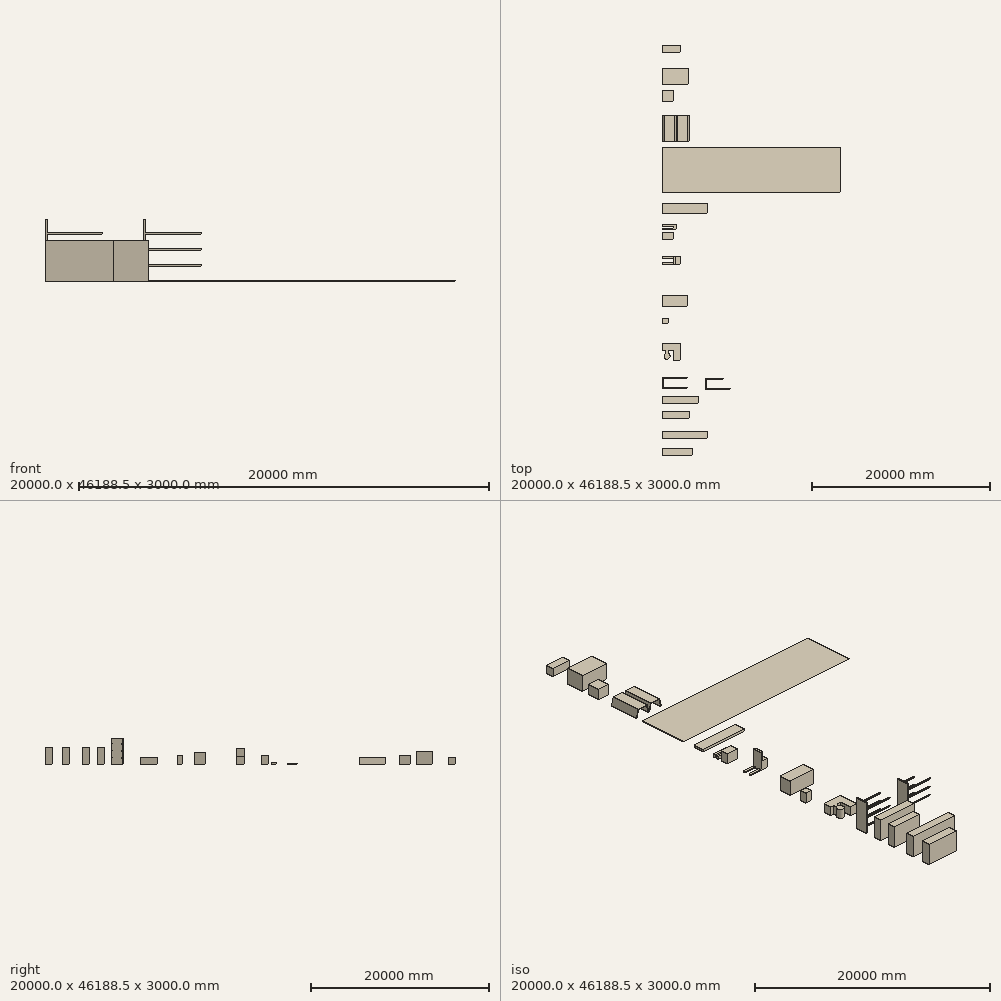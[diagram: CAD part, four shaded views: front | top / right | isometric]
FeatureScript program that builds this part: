
annotation { "Feature Type Name" : "Feature", "Feature Type Description" : "" }
export const myFeature = defineFeature(function(context is Context, id is Id, definition is map)
    precondition{}
    {
        {
            var Q0;
            Q0=qCreatedBy(makeId("Top.planeOp"),FACE);
            var sketch = newSketch(context, id + "F0", { "sketchPlane" : qUnion([Q0])});
            skLineSegment(sketch, "E0.bottom", {"start": v(0, 0) * mm, "end": v(3300, 0) * mm});
            skLineSegment(sketch, "E0.top", {"start": v(0, 800) * mm, "end": v(3300, 800) * mm});
            skLineSegment(sketch, "E0.left", {"start": v(0, 0) * mm, "end": v(0, 800) * mm});
            skLineSegment(sketch, "E0.right", {"start": v(3300, 0) * mm, "end": v(3300, 800) * mm});
            skLineSegment(sketch, "E1", {"start": v(0, 0) * mm, "end": v(0, 21740.58) * mm, "construction": true});
            skLineSegment(sketch, "E2.bottom", {"start": v(0, 1903.16) * mm, "end": v(5020, 1903.16) * mm});
            skLineSegment(sketch, "E2.top", {"start": v(0, 2703.16) * mm, "end": v(5020, 2703.16) * mm});
            skLineSegment(sketch, "E2.left", {"start": v(0, 1903.16) * mm, "end": v(0, 2703.16) * mm});
            skLineSegment(sketch, "E2.right", {"start": v(5020, 1903.16) * mm, "end": v(5020, 2703.16) * mm});
            skLineSegment(sketch, "E3.bottom", {"start": v(0, 4207.9) * mm, "end": v(3010, 4207.9) * mm});
            skLineSegment(sketch, "E3.top", {"start": v(0, 4907.9) * mm, "end": v(3010, 4907.9) * mm});
            skLineSegment(sketch, "E3.left", {"start": v(0, 4207.9) * mm, "end": v(0, 4907.9) * mm});
            skLineSegment(sketch, "E3.right", {"start": v(3010, 4207.9) * mm, "end": v(3010, 4907.9) * mm});
            skLineSegment(sketch, "E4.bottom", {"start": v(0, 5836.08) * mm, "end": v(4010, 5836.08) * mm});
            skLineSegment(sketch, "E4.top", {"start": v(0, 6636.08) * mm, "end": v(4010, 6636.08) * mm});
            skLineSegment(sketch, "E4.left", {"start": v(0, 5836.08) * mm, "end": v(0, 6636.08) * mm});
            skLineSegment(sketch, "E4.right", {"start": v(4010, 5836.08) * mm, "end": v(4010, 6636.08) * mm});
            skLineSegment(sketch, "E5.bottom", {"start": v(0, 7509.41) * mm, "end": v(2800, 7509.41) * mm});
            skLineSegment(sketch, "E5.top", {"start": v(0, 8769.41) * mm, "end": v(2800, 8769.41) * mm});
            skLineSegment(sketch, "E5.left", {"start": v(0, 7509.41) * mm, "end": v(0, 8769.41) * mm});
            skLineSegment(sketch, "E5.right", {"start": v(2800, 7509.41) * mm, "end": v(2800, 8769.41) * mm});
            skLineSegment(sketch, "E6", {"start": v(0, 11853.92) * mm, "end": v(342.53, 11853.92) * mm});
            skLineSegment(sketch, "E7", {"start": v(1200, 11853.92) * mm, "end": v(1200, 10653.92) * mm});
            skLineSegment(sketch, "E8", {"start": v(1200, 10653.92) * mm, "end": v(2000, 10653.92) * mm});
            skLineSegment(sketch, "E9", {"start": v(2000, 10653.92) * mm, "end": v(2000, 12653.92) * mm});
            skLineSegment(sketch, "E10", {"start": v(2000, 12653.92) * mm, "end": v(0, 12653.92) * mm});
            skLineSegment(sketch, "E11", {"start": v(0, 12653.92) * mm, "end": v(0, 11853.92) * mm});
            skArc(sketch, "E12", {"start": v(342.53, 11484.65) * mm, "mid": v(513.67, 10838.01) * mm, "end": v(624.53, 11497.66) * mm});
            skLineSegment(sketch, "E13", {"start": v(342.53, 11853.92) * mm, "end": v(342.53, 11484.65) * mm});
            skLineSegment(sketch, "E14", {"start": v(624.53, 11497.66) * mm, "end": v(624.53, 11853.92) * mm});
            skLineSegment(sketch, "E15.trimOffspring", {"start": v(624.53, 11853.92) * mm, "end": v(1200, 11853.92) * mm});
            skLineSegment(sketch, "E16.bottom", {"start": v(0, 14846.44) * mm, "end": v(630, 14846.44) * mm});
            skLineSegment(sketch, "E16.top", {"start": v(0, 15476.44) * mm, "end": v(630, 15476.44) * mm});
            skLineSegment(sketch, "E16.left", {"start": v(0, 14846.44) * mm, "end": v(0, 15476.44) * mm});
            skLineSegment(sketch, "E16.right", {"start": v(630, 14846.44) * mm, "end": v(630, 15476.44) * mm});
            skLineSegment(sketch, "E17.bottom", {"start": v(0, 16748.95) * mm, "end": v(2800, 16748.95) * mm});
            skLineSegment(sketch, "E17.top", {"start": v(0, 17998.95) * mm, "end": v(2800, 17998.95) * mm});
            skLineSegment(sketch, "E17.left", {"start": v(0, 16748.95) * mm, "end": v(0, 17998.95) * mm});
            skLineSegment(sketch, "E17.right", {"start": v(2800, 16748.95) * mm, "end": v(2800, 17998.95) * mm});
            skLineSegment(sketch, "E18.bottom", {"start": v(0, 21490.58) * mm, "end": v(2000, 21490.58) * mm});
            skLineSegment(sketch, "E18.top", {"start": v(0, 22390.58) * mm, "end": v(2000, 22390.58) * mm});
            skLineSegment(sketch, "E18.left", {"start": v(0, 21490.58) * mm, "end": v(0, 21740.58) * mm});
            skLineSegment(sketch, "E18.right", {"start": v(2000, 21490.58) * mm, "end": v(2000, 22390.58) * mm});
            skLineSegment(sketch, "E19.bottom", {"start": v(0, 21740.58) * mm, "end": v(1200, 21740.58) * mm});
            skLineSegment(sketch, "E19.top", {"start": v(0, 22140.58) * mm, "end": v(1200, 22140.58) * mm});
            skLineSegment(sketch, "E19.right", {"start": v(1200, 21740.58) * mm, "end": v(1200, 22140.58) * mm});
            skLineSegment(sketch, "E20.trimOffspring", {"start": v(0, 22140.58) * mm, "end": v(0, 28687.92) * mm, "construction": true});
            skLineSegment(sketch, "E21.trimOffspring", {"start": v(0, 22140.58) * mm, "end": v(0, 22390.58) * mm});
            skLineSegment(sketch, "E22", {"start": v(2000, 21940.58) * mm, "end": v(-1324.73, 21940.58) * mm, "construction": true});
            skLineSegment(sketch, "E23", {"start": v(0, 25414.25) * mm, "end": v(1500, 25414.25) * mm});
            skLineSegment(sketch, "E24", {"start": v(1500, 25414.25) * mm, "end": v(1500, 26014.25) * mm});
            skLineSegment(sketch, "E25", {"start": v(1500, 26014.25) * mm, "end": v(0, 26014.25) * mm});
            skLineSegment(sketch, "E26", {"start": v(0, 26014.25) * mm, "end": v(0, 25609.33) * mm});
            skLineSegment(sketch, "E27", {"start": v(0, 25609.33) * mm, "end": v(1200, 25609.33) * mm});
            skLineSegment(sketch, "E28", {"start": v(1200, 25804.41) * mm, "end": v(1200, 25609.33) * mm});
            skLineSegment(sketch, "E29", {"start": v(1200, 25804.41) * mm, "end": v(0, 25804.41) * mm});
            skLineSegment(sketch, "E30", {"start": v(0, 25804.41) * mm, "end": v(0, 25414.25) * mm});
            skLineSegment(sketch, "E31.bottom", {"start": v(0, 24312.91) * mm, "end": v(1200, 24312.91) * mm});
            skLineSegment(sketch, "E31.top", {"start": v(0, 25112.91) * mm, "end": v(1200, 25112.91) * mm});
            skLineSegment(sketch, "E31.left", {"start": v(0, 24312.91) * mm, "end": v(0, 25112.91) * mm});
            skLineSegment(sketch, "E31.right", {"start": v(1200, 24312.91) * mm, "end": v(1200, 25112.91) * mm});
            skLineSegment(sketch, "E32", {"start": v(0, 28687.92) * mm, "end": v(0, 48793.29) * mm, "construction": true});
            skLineSegment(sketch, "E33.bottom", {"start": v(0, 27262.66) * mm, "end": v(5000, 27262.66) * mm});
            skLineSegment(sketch, "E33.top", {"start": v(0, 28362.66) * mm, "end": v(5000, 28362.66) * mm});
            skLineSegment(sketch, "E33.left", {"start": v(0, 27262.66) * mm, "end": v(0, 28362.66) * mm});
            skLineSegment(sketch, "E33.right", {"start": v(5000, 27262.66) * mm, "end": v(5000, 28362.66) * mm});
            skLineSegment(sketch, "E34.bottom", {"start": v(0, 29644.15) * mm, "end": v(20000, 29644.15) * mm});
            skLineSegment(sketch, "E34.top", {"start": v(0, 34644.15) * mm, "end": v(20000, 34644.15) * mm});
            skLineSegment(sketch, "E34.left", {"start": v(0, 29644.15) * mm, "end": v(0, 34644.15) * mm});
            skLineSegment(sketch, "E34.right", {"start": v(20000, 29644.15) * mm, "end": v(20000, 34644.15) * mm});
            skLineSegment(sketch, "E35.bottom", {"start": v(0, 35335.06) * mm, "end": v(3000, 35335.06) * mm});
            skLineSegment(sketch, "E35.top", {"start": v(0, 38335.06) * mm, "end": v(3000, 38335.06) * mm});
            skLineSegment(sketch, "E35.left", {"start": v(0, 35335.06) * mm, "end": v(0, 38335.06) * mm});
            skLineSegment(sketch, "E35.right", {"start": v(3000, 35335.06) * mm, "end": v(3000, 38335.06) * mm});
            skLineSegment(sketch, "E36.bottom", {"start": v(0, 39869.72) * mm, "end": v(1200, 39869.72) * mm});
            skLineSegment(sketch, "E36.top", {"start": v(0, 41069.72) * mm, "end": v(1200, 41069.72) * mm});
            skLineSegment(sketch, "E36.left", {"start": v(0, 39869.72) * mm, "end": v(0, 41069.72) * mm});
            skLineSegment(sketch, "E36.right", {"start": v(1200, 39869.72) * mm, "end": v(1200, 41069.72) * mm});
            skLineSegment(sketch, "E37.bottom", {"start": v(0, 46188.53) * mm, "end": v(2000, 46188.53) * mm});
            skLineSegment(sketch, "E37.top", {"start": v(0, 45388.53) * mm, "end": v(2000, 45388.53) * mm});
            skLineSegment(sketch, "E37.left", {"start": v(0, 46188.53) * mm, "end": v(0, 45388.53) * mm});
            skLineSegment(sketch, "E37.right", {"start": v(2000, 46188.53) * mm, "end": v(2000, 45388.53) * mm});
            skSolve(sketch);
        }
        {
            var Q0;
            Q0=makeQuery(id+"F0.imprint","IMPRINT",FACE,{"disambiguationData":[TD([[makeQuery(id+"F0.imprint","IMPRINT",EDGE,{"derivedFrom":sQuery(id+"F0.wireOp",EDGE,"E0.bottom")}),1.0]])]});
            extrude(context, id + "F1", {"entities" : qUnion([Q0]), "depth" : 2000 * mm, "offsetDistance" : 25 * mm});
        }
        {
            var Q0;
            Q0=makeQuery(id+"F0.imprint","IMPRINT",FACE,{"disambiguationData":[TD([[makeQuery(id+"F0.imprint","IMPRINT",EDGE,{"derivedFrom":sQuery(id+"F0.wireOp",EDGE,"E2.bottom")}),1.0]])]});
            extrude(context, id + "F2", {"entities" : qUnion([Q0]), "depth" : 2000 * mm, "offsetDistance" : 25 * mm});
        }
        {
            var Q0;
            Q0=makeQuery(id+"F0.imprint","IMPRINT",FACE,{"disambiguationData":[TD([[makeQuery(id+"F0.imprint","IMPRINT",EDGE,{"derivedFrom":sQuery(id+"F0.wireOp",EDGE,"E3.bottom")}),1.0]])]});
            extrude(context, id + "F3", {"entities" : qUnion([Q0]), "depth" : 2000 * mm, "offsetDistance" : 25 * mm});
        }
        {
            var Q0;
            Q0=makeQuery(id+"F0.imprint","IMPRINT",FACE,{"disambiguationData":[TD([[makeQuery(id+"F0.imprint","IMPRINT",EDGE,{"derivedFrom":sQuery(id+"F0.wireOp",EDGE,"E4.bottom")}),1.0]])]});
            extrude(context, id + "F4", {"entities" : qUnion([Q0]), "depth" : 2000 * mm, "offsetDistance" : 25 * mm});
        }
        {
            var Q0;
            Q0=makeQuery(id+"F0.imprint","IMPRINT",FACE,{"disambiguationData":[TD([[makeQuery(id+"F0.imprint","IMPRINT",EDGE,{"derivedFrom":sQuery(id+"F0.wireOp",EDGE,"E5.bottom")}),1.0]])]});
            extrude(context, id + "F5", {"entities" : qUnion([Q0]), "depth" : 3000 * mm, "offsetDistance" : 25 * mm});
        }
        {
            var Q0;
            Q0=makeQuery(id+"F5.opExtrude","SWEPT_FACE",FACE,{"disambiguationData":[OSD([sQuery(id+"F0.wireOp",EDGE,"E5.top")])]});
            var sketch = newSketch(context, id + "F6", { "sketchPlane" : qUnion([Q0])});
            skLineSegment(sketch, "E38.bottom", {"start": v(-100, 0) * mm, "end": v(-2800, 0) * mm});
            skLineSegment(sketch, "E38.top", {"start": v(-100, 700) * mm, "end": v(-2800, 700) * mm});
            skLineSegment(sketch, "E38.left", {"start": v(-100, 0) * mm, "end": v(-100, 700) * mm});
            skLineSegment(sketch, "E38.right", {"start": v(-2800, 0) * mm, "end": v(-2800, 700) * mm});
            skLineSegment(sketch, "E39.bottom", {"start": v(-100, 800) * mm, "end": v(-2800, 800) * mm});
            skLineSegment(sketch, "E39.top", {"start": v(-100, 1500) * mm, "end": v(-2800, 1500) * mm});
            skLineSegment(sketch, "E39.left", {"start": v(-100, 800) * mm, "end": v(-100, 1500) * mm});
            skLineSegment(sketch, "E39.right", {"start": v(-2800, 800) * mm, "end": v(-2800, 1500) * mm});
            skLineSegment(sketch, "E40.bottom", {"start": v(-100, 1600) * mm, "end": v(-2800, 1600) * mm});
            skLineSegment(sketch, "E40.top", {"start": v(-100, 2300) * mm, "end": v(-2800, 2300) * mm});
            skLineSegment(sketch, "E40.left", {"start": v(-100, 1600) * mm, "end": v(-100, 2300) * mm});
            skLineSegment(sketch, "E40.right", {"start": v(-2800, 1600) * mm, "end": v(-2800, 2300) * mm});
            skLineSegment(sketch, "E41.bottom", {"start": v(-100, 2400) * mm, "end": v(-2800, 2400) * mm});
            skLineSegment(sketch, "E41.top", {"start": v(-100, 3100) * mm, "end": v(-2800, 3100) * mm});
            skLineSegment(sketch, "E41.left", {"start": v(-100, 2400) * mm, "end": v(-100, 3100) * mm});
            skLineSegment(sketch, "E41.right", {"start": v(-2800, 2400) * mm, "end": v(-2800, 3100) * mm});
            skLineSegment(sketch, "E42", {"start": v(-100, 0) * mm, "end": v(-100, 3363.26) * mm, "construction": true});
            skSolve(sketch);
        }
        {
            var Q0;
            Q0 = qSketchRegion(id + "F6", true);
            var Q1;
            Q1=makeQuery(id+"F5.opExtrude","SWEPT_FACE",FACE,{"disambiguationData":[OSD([sQuery(id+"F0.wireOp",EDGE,"E5.bottom")])]});
            extrude(context, id + "F7", {"entities" : qUnion([Q0]), "operationType" : NewBodyOperationType.REMOVE, "endBound" : BoundingType.UP_TO_SURFACE, "oppositeDirection" : true, "depth" : 25 * mm, "endBoundEntityFace" : qUnion([Q1]), "offsetDistance" : 25 * mm});
        }
        {
            var Q0;
            Q0=makeQuery(id+"F7.boolean.opBoolean","COPY",FACE,{"derivedFrom":makeQuery(id+"F7.opExtrude","SWEPT_FACE",FACE,{"disambiguationData":[OSD([sQuery(id+"F6.wireOp",EDGE,"E41.bottom")])]})});
            var sketch = newSketch(context, id + "F8", { "sketchPlane" : qUnion([Q0])});
            skLineSegment(sketch, "E43.bottom", {"start": v(100, 7609.41) * mm, "end": v(3088.05, 7609.41) * mm});
            skLineSegment(sketch, "E43.top", {"start": v(100, 8669.41) * mm, "end": v(3088.05, 8669.41) * mm});
            skLineSegment(sketch, "E43.left", {"start": v(100, 7609.41) * mm, "end": v(100, 8669.41) * mm});
            skLineSegment(sketch, "E43.right", {"start": v(3088.05, 7609.41) * mm, "end": v(3088.05, 8669.41) * mm});
            skSolve(sketch);
        }
        {
            var Q0;
            Q0 = qSketchRegion(id + "F8", true);
            var Q1;
            Q1=makeQuery(id+"F7.boolean.opBoolean","COPY",FACE,{"derivedFrom":makeQuery(id+"F7.opExtrude","SWEPT_FACE",FACE,{"disambiguationData":[OSD([sQuery(id+"F6.wireOp",EDGE,"E38.top")])]})});
            extrude(context, id + "F9", {"entities" : qUnion([Q0]), "operationType" : NewBodyOperationType.REMOVE, "endBound" : BoundingType.UP_TO_SURFACE, "oppositeDirection" : true, "depth" : 25 * mm, "endBoundEntityFace" : qUnion([Q1]), "offsetDistance" : 25 * mm});
        }
        {
            var Q0;
            Q0=makeQuery(id+"F0.imprint","IMPRINT",FACE,{"disambiguationData":[TD([[makeQuery(id+"F0.imprint","IMPRINT",EDGE,{"derivedFrom":sQuery(id+"F0.wireOp",EDGE,"E6")}),1.0]])]});
            extrude(context, id + "F10", {"entities" : qUnion([Q0]), "depth" : 850 * mm, "offsetDistance" : 25 * mm});
        }
        {
            var Q0;
            Q0=makeQuery(id+"F0.imprint","IMPRINT",FACE,{"disambiguationData":[TD([[makeQuery(id+"F0.imprint","IMPRINT",EDGE,{"derivedFrom":sQuery(id+"F0.wireOp",EDGE,"E16.bottom")}),1.0]])]});
            extrude(context, id + "F11", {"entities" : qUnion([Q0]), "depth" : 1000 * mm, "offsetDistance" : 25 * mm});
        }
        {
            var Q0;
            Q0=makeQuery(id+"F0.imprint","IMPRINT",FACE,{"disambiguationData":[TD([[makeQuery(id+"F0.imprint","IMPRINT",EDGE,{"derivedFrom":sQuery(id+"F0.wireOp",EDGE,"E17.bottom")}),1.0]])]});
            extrude(context, id + "F12", {"entities" : qUnion([Q0]), "depth" : 1400 * mm, "offsetDistance" : 25 * mm});
        }
        {
            var Q0;
            Q0=makeQuery(id+"F0.imprint","IMPRINT",FACE,{"disambiguationData":[TD([[makeQuery(id+"F0.imprint","IMPRINT",EDGE,{"derivedFrom":sQuery(id+"F0.wireOp",EDGE,"E18.bottom")}),1.0]])]});
            extrude(context, id + "F13", {"entities" : qUnion([Q0]), "depth" : 1800 * mm, "offsetDistance" : 25 * mm});
        }
        {
            var Q0;
            Q0=makeQuery(id+"F13.opExtrude","SWEPT_FACE",FACE,{"disambiguationData":[OSD([sQuery(id+"F0.wireOp",EDGE,"E18.bottom")])]});
            var sketch = newSketch(context, id + "F14", { "sketchPlane" : qUnion([Q0])});
            skLineSegment(sketch, "E44.bottom", {"start": v(0, 100) * mm, "end": v(1200, 100) * mm});
            skLineSegment(sketch, "E44.top", {"start": v(0, 1800) * mm, "end": v(1200, 1800) * mm});
            skLineSegment(sketch, "E44.left", {"start": v(0, 100) * mm, "end": v(0, 1800) * mm});
            skLineSegment(sketch, "E44.right", {"start": v(1200, 100) * mm, "end": v(1200, 1800) * mm});
            skLineSegment(sketch, "E45.bottom", {"start": v(1396.96, 1800) * mm, "end": v(2000, 1800) * mm});
            skLineSegment(sketch, "E45.top", {"start": v(1396.96, 900) * mm, "end": v(2000, 900) * mm});
            skLineSegment(sketch, "E45.left", {"start": v(1396.96, 1800) * mm, "end": v(1396.96, 900) * mm});
            skLineSegment(sketch, "E45.right", {"start": v(2000, 1800) * mm, "end": v(2000, 900) * mm});
            skSolve(sketch);
        }
        {
            var Q0;
            Q0 = qSketchRegion(id + "F14", true);
            var Q1;
            Q1=makeQuery(id+"F13.opExtrude","SWEPT_FACE",FACE,{"disambiguationData":[OSD([sQuery(id+"F0.wireOp",EDGE,"E18.top")])]});
            extrude(context, id + "F15", {"entities" : qUnion([Q0]), "operationType" : NewBodyOperationType.REMOVE, "endBound" : BoundingType.UP_TO_SURFACE, "oppositeDirection" : true, "depth" : 25 * mm, "endBoundEntityFace" : qUnion([Q1]), "offsetDistance" : 25 * mm});
        }
        {
            var Q0;
            {var subQ0=sQuery(id+"F0.wireOp",EDGE,"E23");Q0=makeQuery(id+"F0.imprint","IMPRINT",FACE,{"disambiguationData":[TD([[makeQuery(id+"F0.imprint","IMPRINT",EDGE,{"derivedFrom":subQ0}),1.0]])]});}
            extrude(context, id + "F16", {"entities" : qUnion([Q0]), "depth" : 300 * mm, "offsetDistance" : 25 * mm});
        }
        {
            var Q0;
            Q0=makeQuery(id+"F0.imprint","IMPRINT",FACE,{"disambiguationData":[TD([[makeQuery(id+"F0.imprint","IMPRINT",EDGE,{"derivedFrom":sQuery(id+"F0.wireOp",EDGE,"E31.bottom")}),1.0]])]});
            extrude(context, id + "F17", {"entities" : qUnion([Q0]), "depth" : 1000 * mm, "offsetDistance" : 25 * mm});
        }
        {
            var Q0;
            Q0=makeQuery(id+"F0.imprint","IMPRINT",FACE,{"disambiguationData":[TD([[makeQuery(id+"F0.imprint","IMPRINT",EDGE,{"derivedFrom":sQuery(id+"F0.wireOp",EDGE,"E33.bottom")}),1.0]])]});
            extrude(context, id + "F18", {"entities" : qUnion([Q0]), "depth" : 200 * mm, "offsetDistance" : 25 * mm});
        }
        {
            var Q0;
            Q0=makeQuery(id+"F0.imprint","IMPRINT",FACE,{"disambiguationData":[TD([[makeQuery(id+"F0.imprint","IMPRINT",EDGE,{"derivedFrom":sQuery(id+"F0.wireOp",EDGE,"E34.bottom")}),1.0]])]});
            extrude(context, id + "F19", {"entities" : qUnion([Q0]), "depth" : 25 * mm, "offsetDistance" : 25 * mm});
        }
        {
            var Q0;
            Q0=makeQuery(id+"F0.imprint","IMPRINT",FACE,{"disambiguationData":[TD([[makeQuery(id+"F0.imprint","IMPRINT",EDGE,{"derivedFrom":sQuery(id+"F0.wireOp",EDGE,"E35.bottom")}),1.0]])]});
            extrude(context, id + "F20", {"entities" : qUnion([Q0]), "depth" : 800 * mm, "offsetDistance" : 25 * mm});
        }
        {
            var Q0;
            Q0=makeQuery(id+"F20.opExtrude","SWEPT_FACE",FACE,{"disambiguationData":[OSD([sQuery(id+"F0.wireOp",EDGE,"E35.bottom")])]});
            var sketch = newSketch(context, id + "F21", { "sketchPlane" : qUnion([Q0])});
            skLineSegment(sketch, "E46", {"start": v(0, 0) * mm, "end": v(214.36, 800) * mm});
            skLineSegment(sketch, "E47", {"start": v(214.36, 800) * mm, "end": v(1285.42, 800) * mm});
            skLineSegment(sketch, "E48", {"start": v(1285.42, 800) * mm, "end": v(1526.64, 0) * mm});
            skLineSegment(sketch, "E49", {"start": v(1526.64, 0) * mm, "end": v(1714.58, 800) * mm});
            skLineSegment(sketch, "E50", {"start": v(1714.58, 800) * mm, "end": v(2785.64, 800) * mm});
            skLineSegment(sketch, "E51", {"start": v(2785.64, 800) * mm, "end": v(3000, 0) * mm});
            skLineSegment(sketch, "E52.0", {"start": v(77.27, -20.7) * mm, "end": v(291.63, 779.3) * mm});
            skLineSegment(sketch, "E53.0", {"start": v(214.36, 720) * mm, "end": v(1285.42, 720) * mm});
            skLineSegment(sketch, "E54.0", {"start": v(2724.25, 720) * mm, "end": v(2922.73, -20.7) * mm});
            skLineSegment(sketch, "E54.1", {"start": v(1777.96, 720) * mm, "end": v(2724.25, 720) * mm});
            skLineSegment(sketch, "E54.2", {"start": v(1608.81, 0) * mm, "end": v(1777.96, 720) * mm});
            skLineSegment(sketch, "E54.3", {"start": v(1208.82, 776.9) * mm, "end": v(1443.08, 0) * mm});
            skLineSegment(sketch, "E55", {"start": v(1443.08, 0) * mm, "end": v(1608.81, 0) * mm});
            skSolve(sketch);
        }
        {
            var Q0;
            {var subQ0=sQuery(id+"F21.wireOp",EDGE,"E46");Q0=makeQuery(id+"F21.imprint","IMPRINT",FACE,{"disambiguationData":[TD([[makeQuery(id+"F21.imprint","IMPRINT",EDGE,{"derivedFrom":subQ0}),1.0]])]});}
            var Q1;
            {var subQ0=sQuery(id+"F21.wireOp",EDGE,"E48");Q1=makeQuery(id+"F21.imprint","IMPRINT",FACE,{"disambiguationData":[TD([[makeQuery(id+"F21.imprint","IMPRINT",EDGE,{"derivedFrom":subQ0}),1.0]])]});}
            var Q2;
            {var subQ0=sQuery(id+"F21.wireOp",EDGE,"E51");Q2=makeQuery(id+"F21.imprint","IMPRINT",FACE,{"disambiguationData":[TD([[makeQuery(id+"F21.imprint","IMPRINT",EDGE,{"derivedFrom":subQ0}),1.0]])]});}
            var Q3;
            {var subQ0=sQuery(id+"F21.wireOp",EDGE,"E53.0");var subQ1=sQuery(id+"F21.wireOp",EDGE,"E52.0");var subQ2=makeQuery(id+"F21.imprint","INTERSECT",VERTEX,{"derivedFrom":[subQ1,subQ0]});Q3=makeQuery(id+"F21.imprint","IMPRINT",FACE,{"disambiguationData":[TD([[makeQuery(id+"F21.imprint","IMPRINT",EDGE,{"disambiguationData":[TD([[subQ2,1.0]])],"derivedFrom":subQ1}),-1.0]])]});}
            var Q4;
            {var subQ0=sQuery(id+"F21.wireOp",EDGE,"E54.1");Q4=makeQuery(id+"F21.imprint","IMPRINT",FACE,{"disambiguationData":[TD([[makeQuery(id+"F21.imprint","IMPRINT",EDGE,{"derivedFrom":subQ0}),-1.0]])]});}
            var Q5;
            Q5=makeQuery(id+"F20.opExtrude","SWEPT_FACE",FACE,{"disambiguationData":[OSD([sQuery(id+"F0.wireOp",EDGE,"E35.top")])]});
            extrude(context, id + "F22", {"entities" : qUnion([Q0, Q1, Q2, Q3, Q4]), "operationType" : NewBodyOperationType.REMOVE, "endBound" : BoundingType.UP_TO_SURFACE, "oppositeDirection" : true, "depth" : 25 * mm, "endBoundEntityFace" : qUnion([Q5]), "offsetDistance" : 25 * mm});
        }
        {
            var Q0;
            Q0=makeQuery(id+"F0.imprint","IMPRINT",FACE,{"disambiguationData":[TD([[makeQuery(id+"F0.imprint","IMPRINT",EDGE,{"derivedFrom":sQuery(id+"F0.wireOp",EDGE,"E36.bottom")}),1.0]])]});
            extrude(context, id + "F23", {"entities" : qUnion([Q0]), "depth" : 1000 * mm, "offsetDistance" : 25 * mm});
        }
        {
            var Q0;
            Q0=makeQuery(id+"F5.opExtrude","SWEPT_BODY",BODY,{"disambiguationData":[OSD([sQuery(id+"F0.wireOp",EDGE,"E5.bottom"),sQuery(id+"F0.wireOp",EDGE,"E5.top"),sQuery(id+"F0.wireOp",EDGE,"E5.left"),sQuery(id+"F0.wireOp",EDGE,"E5.right")])]});
            transform(context, id + "F24", {"entities" : qUnion([Q0]), "transformType" : TransformType.TRANSLATION_3D, "dx" : 4800 * mm, "dy" : -100 * mm, "dz" : 0 * mm, "makeCopy" : true});
        }
        {
            var Q0;
            Q0=makeQuery(id+"F24.opPattern","COPY",FACE,{"derivedFrom":makeQuery(id+"F9.boolean.opBoolean","SPLIT",FACE,{"disambiguationData":[TD([makeQuery(id+"F5.opExtrude","SWEPT_FACE",FACE,{"disambiguationData":[OSD([sQuery(id+"F0.wireOp",EDGE,"E5.bottom")])]})])],"derivedFrom":makeQuery(id+"F7.boolean.opBoolean","COPY",FACE,{"derivedFrom":makeQuery(id+"F7.opExtrude","SWEPT_FACE",FACE,{"disambiguationData":[OSD([sQuery(id+"F6.wireOp",EDGE,"E41.bottom")])]})})}),"instanceName":"1"});
            var sketch = newSketch(context, id + "F25", { "sketchPlane" : qUnion([Q0])});
            skLineSegment(sketch, "E56.bottom", {"start": v(6800, 9228.24) * mm, "end": v(9301.09, 9228.24) * mm});
            skLineSegment(sketch, "E56.top", {"start": v(6800, 6951.24) * mm, "end": v(9301.09, 6951.24) * mm});
            skLineSegment(sketch, "E56.left", {"start": v(6800, 9228.24) * mm, "end": v(6800, 6951.24) * mm});
            skLineSegment(sketch, "E56.right", {"start": v(9301.09, 9228.24) * mm, "end": v(9301.09, 6951.24) * mm});
            skSolve(sketch);
        }
        {
            var Q0;
            {var subQ0=sQuery(id+"F25.wireOp",EDGE,"E56.left");var subQ1=sQuery(id+"F8.wireOp",EDGE,"E43.bottom");var subQ2=makeQuery(id+"F24.opPattern","COPY",EDGE,{"derivedFrom":makeQuery(id+"F9.boolean.opBoolean","COPY",EDGE,{"derivedFrom":makeQuery(id+"F9.opExtrude","CAP_EDGE",EDGE,{"disambiguationData":[OSD([subQ1])],"isStart":true})}),"instanceName":"1"});var subQ3=makeQuery(id+"F25.imprint","INTERSECT",VERTEX,{"derivedFrom":[subQ2,subQ0]});Q0=makeQuery(id+"F25.imprint","IMPRINT",FACE,{"disambiguationData":[TD([[makeQuery(id+"F25.imprint","IMPRINT",EDGE,{"disambiguationData":[TD([[subQ3,-1.0]])],"derivedFrom":subQ0}),1.0]])]});}
            var Q1;
            {var subQ6=sQuery(id+"F25.wireOp",EDGE,"E56.bottom");Q1=makeQuery(id+"F25.imprint","IMPRINT",FACE,{"disambiguationData":[TD([[makeQuery(id+"F25.imprint","IMPRINT",EDGE,{"derivedFrom":subQ6}),-1.0]])]});}
            extrude(context, id + "F26", {"entities" : qUnion([Q0, Q1]), "operationType" : NewBodyOperationType.REMOVE, "oppositeDirection" : true, "depth" : 2700 * mm, "offsetDistance" : 25 * mm});
        }
        {
            var Q0;
            Q0=qCreatedBy(makeId("Top.planeOp"),FACE);
            var sketch = newSketch(context, id + "F27", { "sketchPlane" : qUnion([Q0])});
            skLineSegment(sketch, "E57.bottom", {"start": v(0, 41826.89) * mm, "end": v(2900, 41826.89) * mm});
            skLineSegment(sketch, "E57.top", {"start": v(0, 43626.89) * mm, "end": v(2900, 43626.89) * mm});
            skLineSegment(sketch, "E57.left", {"start": v(0, 41826.89) * mm, "end": v(0, 43626.89) * mm});
            skLineSegment(sketch, "E57.right", {"start": v(2900, 41826.89) * mm, "end": v(2900, 43626.89) * mm});
            skSolve(sketch);
        }
        {
            var Q0;
            Q0=makeQuery(id+"F27.imprint","IMPRINT",FACE,{"disambiguationData":[TD([[makeQuery(id+"F27.imprint","IMPRINT",EDGE,{"derivedFrom":sQuery(id+"F27.wireOp",EDGE,"E57.bottom")}),1.0]])]});
            extrude(context, id + "F28", {"entities" : qUnion([Q0]), "depth" : 1550 * mm, "offsetDistance" : 25 * mm});
        }
        {
            var Q0;
            Q0=makeQuery(id+"F0.imprint","IMPRINT",FACE,{"disambiguationData":[TD([[makeQuery(id+"F0.imprint","IMPRINT",EDGE,{"derivedFrom":sQuery(id+"F0.wireOp",EDGE,"E37.bottom")}),-1.0]])]});
            extrude(context, id + "F29", {"entities" : qUnion([Q0]), "depth" : 800 * mm, "offsetDistance" : 25 * mm});
        }
    });
